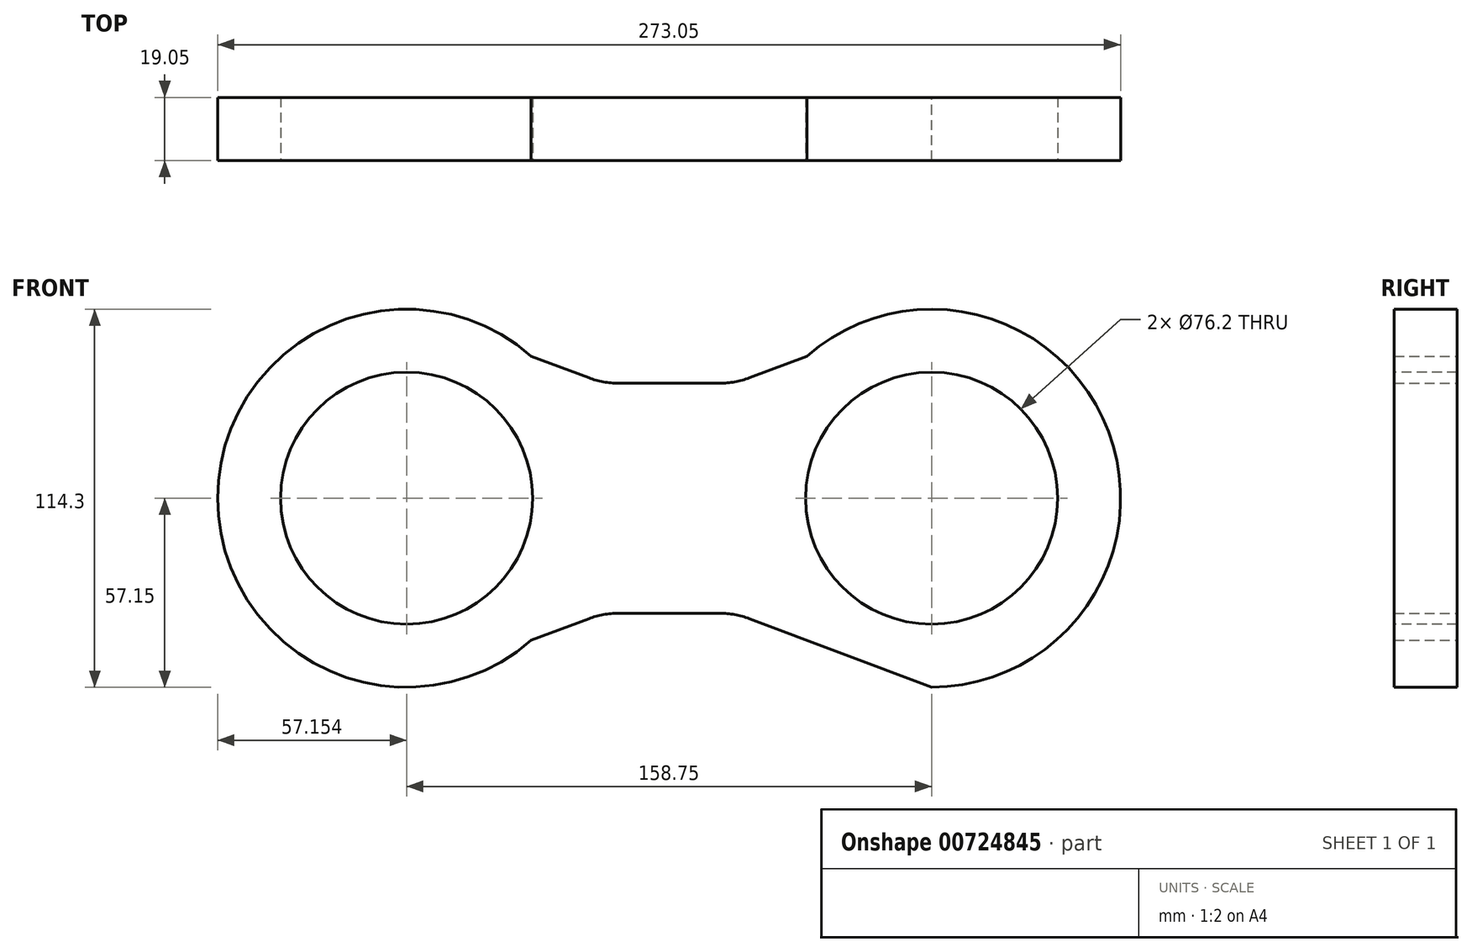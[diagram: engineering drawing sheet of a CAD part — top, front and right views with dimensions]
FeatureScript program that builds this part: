
annotation { "Feature Type Name" : "Feature", "Feature Type Description" : "" }
export const myFeature = defineFeature(function(context is Context, id is Id, definition is map)
    precondition{}
    {
        {
            var Q0;
            Q0=qCreatedBy(makeId("Front.planeOp"),FACE);
            var sketch = newSketch(context, id + "F0", { "sketchPlane" : qUnion([Q0])});
            skCircle(sketch, "E0", {"center": v(-35.08, 0) * mm, "radius": 57.15 * mm});
            skCircle(sketch, "E1", {"center": v(123.67, 0) * mm, "radius": 57.15 * mm});
            skLineSegment(sketch, "E2", {"start": v(-35.08, 57.15) * mm, "end": v(20.03, 36.4) * mm});
            skLineSegment(sketch, "E3", {"start": v(28.98, 34.78) * mm, "end": v(59.62, 34.78) * mm});
            skLineSegment(sketch, "E4", {"start": v(68.57, 36.4) * mm, "end": v(123.67, 57.15) * mm});
            skLineSegment(sketch, "E5", {"start": v(-35.08, -57.15) * mm, "end": v(20.03, -36.4) * mm});
            skLineSegment(sketch, "E6", {"start": v(28.98, -34.78) * mm, "end": v(59.62, -34.78) * mm});
            skLineSegment(sketch, "E7", {"start": v(68.57, -36.4) * mm, "end": v(123.67, -57.15) * mm});
            skPoint(sketch, "E8.visualSharp", {"position": v(24.35, 34.78) * mm});
            skArc(sketch, "E8.filletArc", {"start": v(20.03, 36.4) * mm, "mid": v(24.43, 35.19) * mm, "end": v(28.98, 34.78) * mm});
            skPoint(sketch, "E9.visualSharp", {"position": v(64.25, 34.78) * mm});
            skArc(sketch, "E9.filletArc", {"start": v(59.62, 34.78) * mm, "mid": v(64.17, 35.19) * mm, "end": v(68.57, 36.4) * mm});
            skPoint(sketch, "E10.visualSharp", {"position": v(24.35, -34.78) * mm});
            skArc(sketch, "E10.filletArc", {"start": v(28.98, -34.78) * mm, "mid": v(24.43, -35.19) * mm, "end": v(20.03, -36.4) * mm});
            skPoint(sketch, "E11.visualSharp", {"position": v(64.25, -34.78) * mm});
            skArc(sketch, "E11.filletArc", {"start": v(68.57, -36.4) * mm, "mid": v(64.17, -35.19) * mm, "end": v(59.62, -34.78) * mm});
            skSolve(sketch);
        }
        {
            var Q0;
            Q0=makeQuery(id+"F0.imprint","IMPRINT",FACE,{"disambiguationData":[TD([[makeQuery(id+"F0.imprint","IMPRINT",EDGE,{"derivedFrom":sQuery(id+"F0.wireOp",EDGE,"E3")}),-1.0]])]});
            var Q1;
            {var subQ0=sQuery(id+"F0.wireOp",EDGE,"E2");var subQ1=sQuery(id+"F0.wireOp",EDGE,"E0");var subQ2=makeQuery(id+"F0.imprint","INTERSECT",VERTEX,{"disambiguationData":[OD(0.0)],"derivedFrom":[subQ1,subQ0]});Q1=makeQuery(id+"F0.imprint","IMPRINT",FACE,{"disambiguationData":[TD([[makeQuery(id+"F0.imprint","IMPRINT",EDGE,{"disambiguationData":[TD([[subQ2,-1.0]])],"derivedFrom":subQ1}),1.0]])]});}
            var Q2;
            {var subQ0=sQuery(id+"F0.wireOp",EDGE,"E4");var subQ1=sQuery(id+"F0.wireOp",EDGE,"E1");var subQ2=makeQuery(id+"F0.imprint","INTERSECT",VERTEX,{"disambiguationData":[OD(1.0)],"derivedFrom":[subQ1,subQ0]});Q2=makeQuery(id+"F0.imprint","IMPRINT",FACE,{"disambiguationData":[TD([[makeQuery(id+"F0.imprint","IMPRINT",EDGE,{"disambiguationData":[TD([[subQ2,-1.0]])],"derivedFrom":subQ1}),1.0]])]});}
            var Q3;
            {var subQ0=sQuery(id+"F0.wireOp",EDGE,"E4");var subQ1=sQuery(id+"F0.wireOp",EDGE,"E1");var subQ2=makeQuery(id+"F0.imprint","INTERSECT",VERTEX,{"disambiguationData":[OD(0.0)],"derivedFrom":[subQ1,subQ0]});Q3=makeQuery(id+"F0.imprint","IMPRINT",FACE,{"disambiguationData":[TD([[makeQuery(id+"F0.imprint","IMPRINT",EDGE,{"disambiguationData":[TD([[subQ2,-1.0]])],"derivedFrom":subQ1}),1.0]])]});}
            var Q4;
            {var subQ0=sQuery(id+"F0.wireOp",EDGE,"E2");var subQ1=sQuery(id+"F0.wireOp",EDGE,"E0");var subQ2=makeQuery(id+"F0.imprint","INTERSECT",VERTEX,{"disambiguationData":[OD(0.0)],"derivedFrom":[subQ1,subQ0]});Q4=makeQuery(id+"F0.imprint","IMPRINT",FACE,{"disambiguationData":[TD([[makeQuery(id+"F0.imprint","IMPRINT",EDGE,{"disambiguationData":[TD([[subQ2,1.0]])],"derivedFrom":subQ1}),1.0]])]});}
            var Q5;
            {var subQ0=sQuery(id+"F0.wireOp",EDGE,"E5");var subQ1=sQuery(id+"F0.wireOp",EDGE,"E0");var subQ2=makeQuery(id+"F0.imprint","INTERSECT",VERTEX,{"disambiguationData":[OD(0.0)],"derivedFrom":[subQ1,subQ0]});Q5=makeQuery(id+"F0.imprint","IMPRINT",FACE,{"disambiguationData":[TD([[makeQuery(id+"F0.imprint","IMPRINT",EDGE,{"disambiguationData":[TD([[subQ2,-1.0]])],"derivedFrom":subQ1}),1.0]])]});}
            var Q6;
            {var subQ0=sQuery(id+"F0.wireOp",EDGE,"E7");var subQ1=sQuery(id+"F0.wireOp",EDGE,"E1");var subQ2=makeQuery(id+"F0.imprint","INTERSECT",VERTEX,{"disambiguationData":[OD(0.0)],"derivedFrom":[subQ1,subQ0]});Q6=makeQuery(id+"F0.imprint","IMPRINT",FACE,{"disambiguationData":[TD([[makeQuery(id+"F0.imprint","IMPRINT",EDGE,{"disambiguationData":[TD([[subQ2,1.0]])],"derivedFrom":subQ1}),1.0]])]});}
            extrude(context, id + "F1", {"entities" : qUnion([Q0, Q1, Q2, Q3, Q4, Q5, Q6]), "depth" : 19.05 * mm, "offsetDistance" : 25.4 * mm});
        }
        {
            var Q0;
            Q0=makeQuery(id+"F1.opExtrude","CAP_FACE",FACE,{"disambiguationData":[OSD([sQuery(id+"F0.wireOp",EDGE,"E0"),sQuery(id+"F0.wireOp",EDGE,"E1"),sQuery(id+"F0.wireOp",EDGE,"E2"),sQuery(id+"F0.wireOp",EDGE,"E3"),sQuery(id+"F0.wireOp",EDGE,"E4"),sQuery(id+"F0.wireOp",EDGE,"E5"),sQuery(id+"F0.wireOp",EDGE,"E6"),sQuery(id+"F0.wireOp",EDGE,"E7"),sQuery(id+"F0.wireOp",EDGE,"E8.filletArc"),sQuery(id+"F0.wireOp",EDGE,"E9.filletArc"),sQuery(id+"F0.wireOp",EDGE,"E10.filletArc"),sQuery(id+"F0.wireOp",EDGE,"E11.filletArc")])],"isStart":false});
            var sketch = newSketch(context, id + "F2", { "sketchPlane" : qUnion([Q0])});
            skCircle(sketch, "E12", {"center": v(-35.08, 0) * mm, "radius": 38.1 * mm});
            skCircle(sketch, "E13", {"center": v(123.67, 0) * mm, "radius": 38.1 * mm});
            skSolve(sketch);
        }
        {
            var Q0;
            Q0=makeQuery(id+"F2.imprint","IMPRINT",FACE,{"disambiguationData":[TD([[makeQuery(id+"F2.imprint","IMPRINT",EDGE,{"derivedFrom":sQuery(id+"F2.wireOp",EDGE,"E12")}),1.0]])]});
            var Q1;
            Q1=makeQuery(id+"F2.imprint","IMPRINT",FACE,{"disambiguationData":[TD([[makeQuery(id+"F2.imprint","IMPRINT",EDGE,{"derivedFrom":sQuery(id+"F2.wireOp",EDGE,"E13")}),1.0]])]});
            extrude(context, id + "F3", {"entities" : qUnion([Q0, Q1]), "operationType" : NewBodyOperationType.REMOVE, "oppositeDirection" : true, "depth" : 25.4 * mm, "offsetDistance" : 25.4 * mm});
        }
    });
